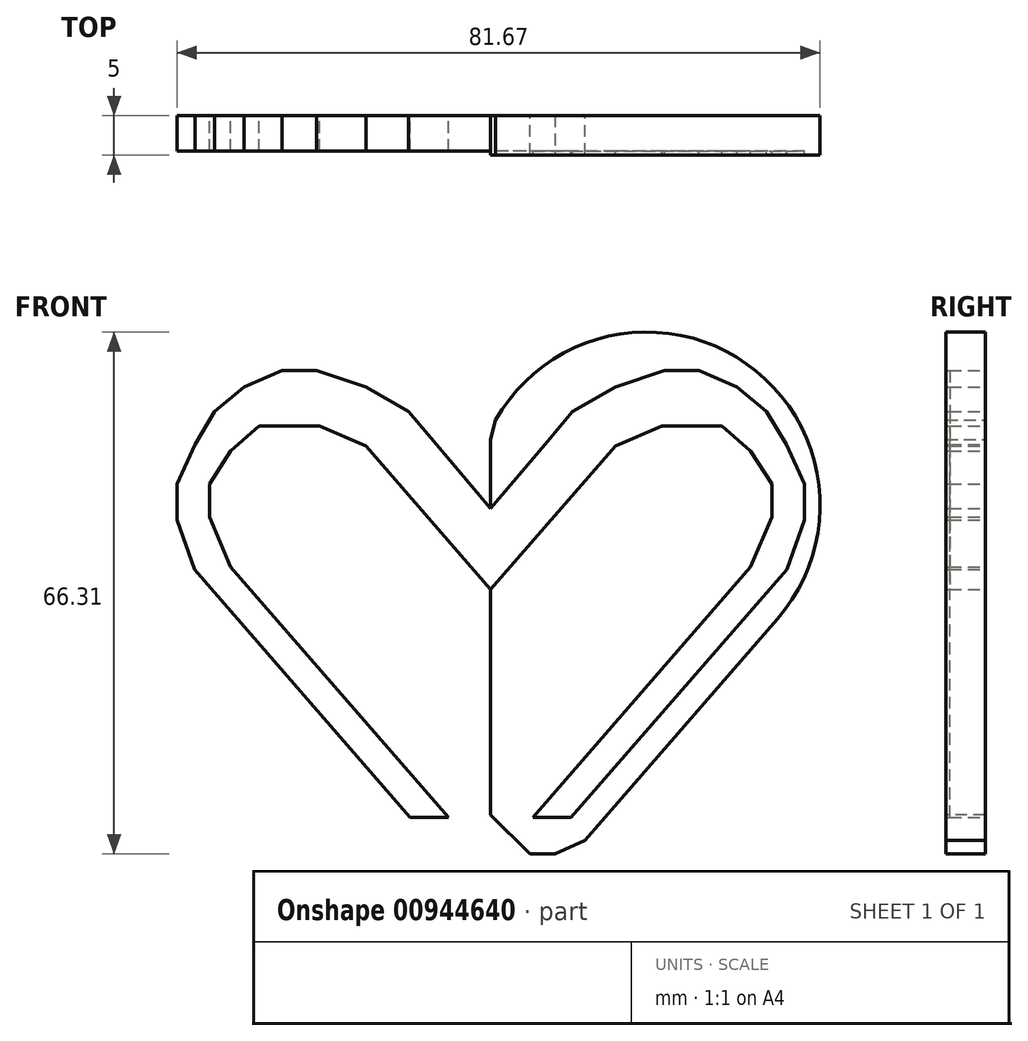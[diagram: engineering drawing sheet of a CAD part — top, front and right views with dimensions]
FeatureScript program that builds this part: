
annotation { "Feature Type Name" : "Feature", "Feature Type Description" : "" }
export const myFeature = defineFeature(function(context is Context, id is Id, definition is map)
    precondition{}
    {
        {
            var Q0;
            Q0=qCreatedBy(makeId("Front.planeOp"),FACE);
            var sketch = newSketch(context, id + "F0", { "sketchPlane" : qUnion([Q0])});
            skLineSegment(sketch, "E0", {"start": v(0, 55.6) * mm, "end": v(0, -55) * mm});
            skArc(sketch, "E1", {"start": v(36.43, 1.09) * mm, "mid": v(31.95, 33.91) * mm, "end": v(0, 25.15) * mm});
            skLineSegment(sketch, "E2", {"start": v(36.43, 1.09) * mm, "end": v(0, -40.78) * mm});
            skArc(sketch, "E3.MirrorCS", {"start": v(-36.43, 1.09) * mm, "mid": v(-31.95, 33.91) * mm, "end": v(0, 25.15) * mm});
            skLineSegment(sketch, "E4.MirrorCS", {"start": v(-36.43, 1.09) * mm, "end": v(0, -40.78) * mm});
            skLineSegment(sketch, "E5", {"start": v(-32.16, -28.75) * mm, "end": v(38.37, -28.75) * mm});
            skLineSegment(sketch, "E6", {"start": v(-10.22, -24.1) * mm, "end": v(-17.53, -15.7) * mm});
            skLineSegment(sketch, "E7", {"start": v(-17.53, -15.7) * mm, "end": v(-37.62, 7.4) * mm});
            skLineSegment(sketch, "E8", {"start": v(-37.62, 7.4) * mm, "end": v(-39.84, 13.66) * mm});
            skLineSegment(sketch, "E9", {"start": v(-39.84, 13.66) * mm, "end": v(-39.84, 18.25) * mm});
            skLineSegment(sketch, "E10", {"start": v(-39.84, 18.25) * mm, "end": v(-37.55, 23.26) * mm});
            skLineSegment(sketch, "E11", {"start": v(-37.55, 23.26) * mm, "end": v(-35.05, 27.43) * mm});
            skLineSegment(sketch, "E12", {"start": v(-35.05, 27.43) * mm, "end": v(-31.3, 30.56) * mm});
            skLineSegment(sketch, "E13", {"start": v(-31.3, 30.56) * mm, "end": v(-26.5, 32.65) * mm});
            skLineSegment(sketch, "E14", {"start": v(-26.5, 32.65) * mm, "end": v(-22.11, 32.65) * mm});
            skLineSegment(sketch, "E15", {"start": v(-22.11, 32.65) * mm, "end": v(-15.85, 30.56) * mm});
            skLineSegment(sketch, "E16", {"start": v(-15.85, 30.56) * mm, "end": v(-10.43, 27.43) * mm});
            skLineSegment(sketch, "E17", {"start": v(-10.43, 27.43) * mm, "end": v(-6.88, 23.26) * mm});
            skLineSegment(sketch, "E18", {"start": v(-6.88, 23.26) * mm, "end": v(0, 15.12) * mm});
            skLineSegment(sketch, "E19.MirrorCS", {"start": v(10.22, -24.1) * mm, "end": v(17.53, -15.7) * mm});
            skLineSegment(sketch, "E20.MirrorCS", {"start": v(17.53, -15.7) * mm, "end": v(37.62, 7.4) * mm});
            skLineSegment(sketch, "E21.MirrorCS", {"start": v(37.62, 7.4) * mm, "end": v(39.84, 13.66) * mm});
            skLineSegment(sketch, "E22.MirrorCS", {"start": v(39.84, 13.66) * mm, "end": v(39.84, 18.25) * mm});
            skLineSegment(sketch, "E23.MirrorCS", {"start": v(39.84, 18.25) * mm, "end": v(37.55, 23.26) * mm});
            skLineSegment(sketch, "E24.MirrorCS", {"start": v(37.55, 23.26) * mm, "end": v(35.05, 27.43) * mm});
            skLineSegment(sketch, "E25.MirrorCS", {"start": v(35.05, 27.43) * mm, "end": v(31.3, 30.56) * mm});
            skLineSegment(sketch, "E26.MirrorCS", {"start": v(31.3, 30.56) * mm, "end": v(26.5, 32.65) * mm});
            skLineSegment(sketch, "E27.MirrorCS", {"start": v(26.5, 32.65) * mm, "end": v(22.11, 32.65) * mm});
            skLineSegment(sketch, "E28.MirrorCS", {"start": v(22.11, 32.65) * mm, "end": v(15.85, 30.56) * mm});
            skLineSegment(sketch, "E29.MirrorCS", {"start": v(15.85, 30.56) * mm, "end": v(10.43, 27.43) * mm});
            skLineSegment(sketch, "E30.MirrorCS", {"start": v(10.43, 27.43) * mm, "end": v(6.88, 23.26) * mm});
            skLineSegment(sketch, "E31.MirrorCS", {"start": v(6.88, 23.26) * mm, "end": v(0, 15.12) * mm});
            skLineSegment(sketch, "E32", {"start": v(-5.36, -24.1) * mm, "end": v(-12.6, -15.77) * mm});
            skLineSegment(sketch, "E33", {"start": v(-12.6, -15.77) * mm, "end": v(-33.04, 7.71) * mm});
            skLineSegment(sketch, "E34", {"start": v(-33.04, 7.71) * mm, "end": v(-35.71, 14.05) * mm});
            skLineSegment(sketch, "E35", {"start": v(-35.71, 14.05) * mm, "end": v(-35.71, 18.25) * mm});
            skLineSegment(sketch, "E36", {"start": v(-35.71, 18.25) * mm, "end": v(-33.04, 22.47) * mm});
            skLineSegment(sketch, "E37", {"start": v(-33.04, 22.47) * mm, "end": v(-29.4, 25.63) * mm});
            skLineSegment(sketch, "E38", {"start": v(-29.4, 25.63) * mm, "end": v(-25.3, 25.63) * mm});
            skLineSegment(sketch, "E39", {"start": v(-25.3, 25.63) * mm, "end": v(-21.75, 25.63) * mm});
            skLineSegment(sketch, "E40", {"start": v(-21.75, 25.63) * mm, "end": v(-15.85, 23.06) * mm});
            skLineSegment(sketch, "E41", {"start": v(-15.85, 23.06) * mm, "end": v(-11.67, 18.25) * mm});
            skLineSegment(sketch, "E42", {"start": v(-11.67, 18.25) * mm, "end": v(-7.68, 13.66) * mm});
            skLineSegment(sketch, "E43", {"start": v(-7.68, 13.66) * mm, "end": v(-2.5, 7.71) * mm});
            skLineSegment(sketch, "E44", {"start": v(-2.5, 7.71) * mm, "end": v(0, 4.84) * mm});
            skLineSegment(sketch, "E45", {"start": v(-10.22, -24.1) * mm, "end": v(-5.36, -24.1) * mm});
            skLineSegment(sketch, "E46.MirrorCS", {"start": v(10.22, -24.1) * mm, "end": v(5.36, -24.1) * mm});
            skLineSegment(sketch, "E47.MirrorCS", {"start": v(5.36, -24.1) * mm, "end": v(12.6, -15.77) * mm});
            skLineSegment(sketch, "E48.MirrorCS", {"start": v(12.6, -15.77) * mm, "end": v(33.04, 7.71) * mm});
            skLineSegment(sketch, "E49.MirrorCS", {"start": v(33.04, 7.71) * mm, "end": v(35.71, 14.05) * mm});
            skLineSegment(sketch, "E50.MirrorCS", {"start": v(35.71, 14.05) * mm, "end": v(35.71, 18.25) * mm});
            skLineSegment(sketch, "E51.MirrorCS", {"start": v(35.71, 18.25) * mm, "end": v(33.04, 22.47) * mm});
            skLineSegment(sketch, "E52.MirrorCS", {"start": v(33.04, 22.47) * mm, "end": v(29.4, 25.63) * mm});
            skLineSegment(sketch, "E53.MirrorCS", {"start": v(29.4, 25.63) * mm, "end": v(25.3, 25.63) * mm});
            skLineSegment(sketch, "E54.MirrorCS", {"start": v(25.3, 25.63) * mm, "end": v(21.75, 25.63) * mm});
            skLineSegment(sketch, "E55.MirrorCS", {"start": v(21.75, 25.63) * mm, "end": v(15.85, 23.06) * mm});
            skLineSegment(sketch, "E56.MirrorCS", {"start": v(15.85, 23.06) * mm, "end": v(11.67, 18.25) * mm});
            skLineSegment(sketch, "E57.MirrorCS", {"start": v(11.67, 18.25) * mm, "end": v(7.68, 13.66) * mm});
            skLineSegment(sketch, "E58.MirrorCS", {"start": v(7.68, 13.66) * mm, "end": v(2.5, 7.71) * mm});
            skLineSegment(sketch, "E59.MirrorCS", {"start": v(2.5, 7.71) * mm, "end": v(0, 4.84) * mm});
            skSolve(sketch);
        }
        {
            var Q0;
            {var subQ1=sQuery(id+"F0.wireOp",EDGE,"E1");Q0=makeQuery(id+"F0.imprint","IMPRINT",FACE,{"disambiguationData":[TD([[makeQuery(id+"F0.imprint","IMPRINT",EDGE,{"derivedFrom":subQ1}),1.0]])]});}
            var Q1;
            {var subQ2=sQuery(id+"F0.wireOp",EDGE,"E3.MirrorCS");Q1=makeQuery(id+"F0.imprint","IMPRINT",FACE,{"disambiguationData":[TD([[makeQuery(id+"F0.imprint","IMPRINT",EDGE,{"derivedFrom":subQ2}),-1.0]])]});}
            extrude(context, id + "F1", {"entities" : qUnion([Q0, Q1]), "depth" : 5 * mm, "offsetDistance" : 25 * mm});
        }
        {
            var Q0;
            Q0=makeQuery(id+"F1.opExtrude","SWEPT_EDGE",EDGE,{"disambiguationData":[OSD([sQuery(id+"F0.wireOp",EDGE,"E0"),sQuery(id+"F0.wireOp",EDGE,"E1"),sQuery(id+"F0.wireOp",EDGE,"E3.MirrorCS")])]});
            var Q1;
            Q1=makeQuery(id+"F1.opExtrude","SWEPT_EDGE",EDGE,{"disambiguationData":[OSD([sQuery(id+"F0.wireOp",EDGE,"E4.MirrorCS"),sQuery(id+"F0.wireOp",EDGE,"E5")])]});
            var Q2;
            Q2=makeQuery(id+"F1.opExtrude","SWEPT_EDGE",EDGE,{"disambiguationData":[OSD([sQuery(id+"F0.wireOp",EDGE,"E2"),sQuery(id+"F0.wireOp",EDGE,"E5")])]});
            chamfer(context, id + "F2", {"entities" : qUnion([Q0, Q1, Q2]), "width" : 5 * mm, "tangentPropagation" : true});
        }
        {
            var Q0;
            Q0=makeQuery(id+"F0.imprint","IMPRINT",FACE,{"disambiguationData":[TD([[makeQuery(id+"F0.imprint","IMPRINT",EDGE,{"derivedFrom":sQuery(id+"F0.wireOp",EDGE,"E6")}),-1.0]])]});
            var Q1;
            Q1=makeQuery(id+"F0.imprint","IMPRINT",FACE,{"disambiguationData":[TD([[makeQuery(id+"F0.imprint","IMPRINT",EDGE,{"derivedFrom":sQuery(id+"F0.wireOp",EDGE,"E19.MirrorCS")}),1.0]])]});
            extrude(context, id + "F3", {"entities" : qUnion([Q0, Q1]), "operationType" : NewBodyOperationType.ADD, "depth" : 4.5 * mm, "offsetDistance" : 25 * mm});
        }
    });
